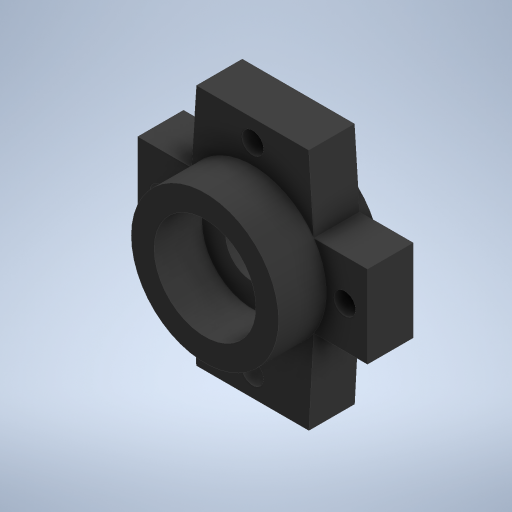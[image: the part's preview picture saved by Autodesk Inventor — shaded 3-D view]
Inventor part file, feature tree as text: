
AUTODESK INVENTOR PART (.ipt)
format: ipt  version: 2023.1 (Build 271208000, 208)  size: 498,688 bytes
history: native  units: mm
features: sketch x11, extrude x11, other x1, fillet x1
ambient origin geometry x8: Origin, YZ Plane, XZ Plane, XY Plane, X Axis, Y Axis, Z Axis, Center Point
bodies: Body1 (feature_tree)
feature tree (24):
  other  "솔리드1"
  sketch  "스케치1"
  extrude  "돌출1"  Depth=5.0mm
  extrude  "돌출2"  Depth=1.9mm
  extrude  "돌출3"  Depth=16.5mm
  extrude  "돌출4"  Depth=29.0mm
  extrude  "돌출5"  Depth=1.0mm
  sketch  "스케치4"
  extrude  "돌출6"  Depth=1.0mm
  extrude  "돌출7"  Depth=1.0mm
  extrude  "돌출8"  Depth=1.0mm
  extrude  "돌출9"  Depth=10.0mm
  extrude  "돌출10"  Depth=10.0mm
  fillet  "모깎기1"  Radius=16.6mm
  sketch  "스케치11"
  extrude  "돌출11"  Depth=14.0mm
  sketch  "스케치2"
  sketch  "스케치3"
  sketch  "스케치5"
  sketch  "스케치6"
  sketch  "스케치7"
  sketch  "스케치9"
  sketch  "스케치10"
  sketch  "스케치12"
